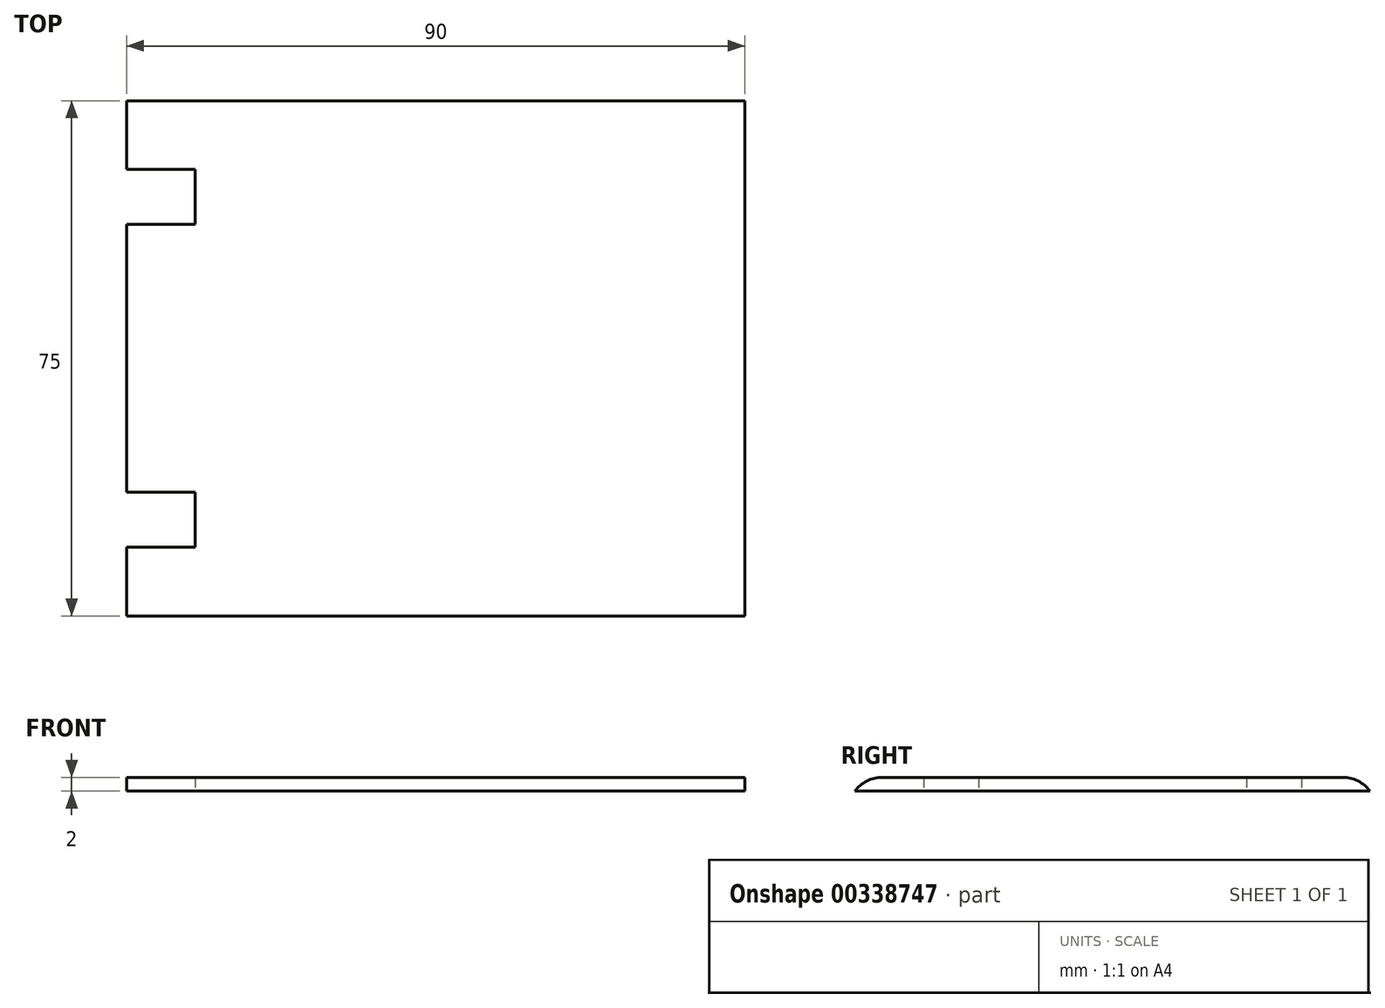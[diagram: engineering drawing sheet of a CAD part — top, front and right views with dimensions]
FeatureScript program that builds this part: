
annotation { "Feature Type Name" : "Feature", "Feature Type Description" : "" }
export const myFeature = defineFeature(function(context is Context, id is Id, definition is map)
    precondition{}
    {
        {
            var Q0;
            Q0=qCreatedBy(makeId("Top.planeOp"),FACE);
            var sketch = newSketch(context, id + "F0", { "sketchPlane" : qUnion([Q0])});
            skLineSegment(sketch, "E0.bottom", {"start": v(-45, 27.5) * mm, "end": v(45, 27.5) * mm});
            skLineSegment(sketch, "E0.top", {"start": v(-45, -27.5) * mm, "end": v(45, -27.5) * mm});
            skLineSegment(sketch, "E0.left", {"start": v(-45, 27.5) * mm, "end": v(-45, -27.5) * mm});
            skLineSegment(sketch, "E0.right", {"start": v(45, 27.5) * mm, "end": v(45, -27.5) * mm});
            skPoint(sketch, "E0.middle", {"position": v(0, 0) * mm});
            skLineSegment(sketch, "E1", {"start": v(-45, 19.5) * mm, "end": v(-35, 19.5) * mm});
            skLineSegment(sketch, "E2", {"start": v(-35, 19.5) * mm, "end": v(-35, 27.5) * mm});
            skLineSegment(sketch, "E3.MirrorCS", {"start": v(-45, -19.5) * mm, "end": v(-35, -19.5) * mm});
            skLineSegment(sketch, "E4.MirrorCS", {"start": v(-35, -19.5) * mm, "end": v(-35, -27.5) * mm});
            skLineSegment(sketch, "E5.MirrorCS", {"start": v(-45, -27.5) * mm, "end": v(-45, 27.5) * mm});
            skLineSegment(sketch, "E6", {"start": v(-45, 27.5) * mm, "end": v(-45, 37.5) * mm});
            skLineSegment(sketch, "E7", {"start": v(-45, 37.5) * mm, "end": v(45, 37.5) * mm});
            skLineSegment(sketch, "E8", {"start": v(45, 37.5) * mm, "end": v(45, 27.5) * mm});
            skLineSegment(sketch, "E9.MirrorCS", {"start": v(-45, -37.5) * mm, "end": v(45, -37.5) * mm});
            skLineSegment(sketch, "E10.MirrorCS", {"start": v(45, -37.5) * mm, "end": v(45, -27.5) * mm});
            skLineSegment(sketch, "E11.MirrorCS", {"start": v(-45, -27.5) * mm, "end": v(-45, -37.5) * mm});
            skSolve(sketch);
        }
        {
            var Q0;
            {var subQ2=sQuery(id+"F0.wireOp",EDGE,"E0.right");Q0=makeQuery(id+"F0.imprint","IMPRINT",FACE,{"disambiguationData":[TD([[makeQuery(id+"F0.imprint","IMPRINT",EDGE,{"derivedFrom":subQ2}),-1.0]])]});}
            var Q1;
            {var subQ0=sQuery(id+"F0.wireOp",EDGE,"E6");Q1=makeQuery(id+"F0.imprint","IMPRINT",FACE,{"disambiguationData":[TD([[makeQuery(id+"F0.imprint","IMPRINT",EDGE,{"derivedFrom":subQ0}),-1.0]])]});}
            var Q2;
            Q2=makeQuery(id+"F0.imprint","IMPRINT",FACE,{"disambiguationData":[TD([[makeQuery(id+"F0.imprint","IMPRINT",EDGE,{"derivedFrom":sQuery(id+"F0.wireOp",EDGE,"E9.MirrorCS")}),1.0]])]});
            extrude(context, id + "F1", {"entities" : qUnion([Q0, Q1, Q2]), "depth" : 2 * mm});
        }
        {
            var Q0;
            Q0=makeQuery(id+"F1.opExtrude","CAP_EDGE",EDGE,{"disambiguationData":[OSD([sQuery(id+"F0.wireOp",EDGE,"E7")])],"isStart":false});
            var Q1;
            Q1=makeQuery(id+"F1.opExtrude","CAP_EDGE",EDGE,{"disambiguationData":[OSD([sQuery(id+"F0.wireOp",EDGE,"E9.MirrorCS")])],"isStart":false});
            fillet(context, id + "F2", {"entities" : qUnion([Q0, Q1]), "radius" : 5 * mm, "tangentPropagation" : true, "allowEdgeOverflow" : false});
        }
    });
